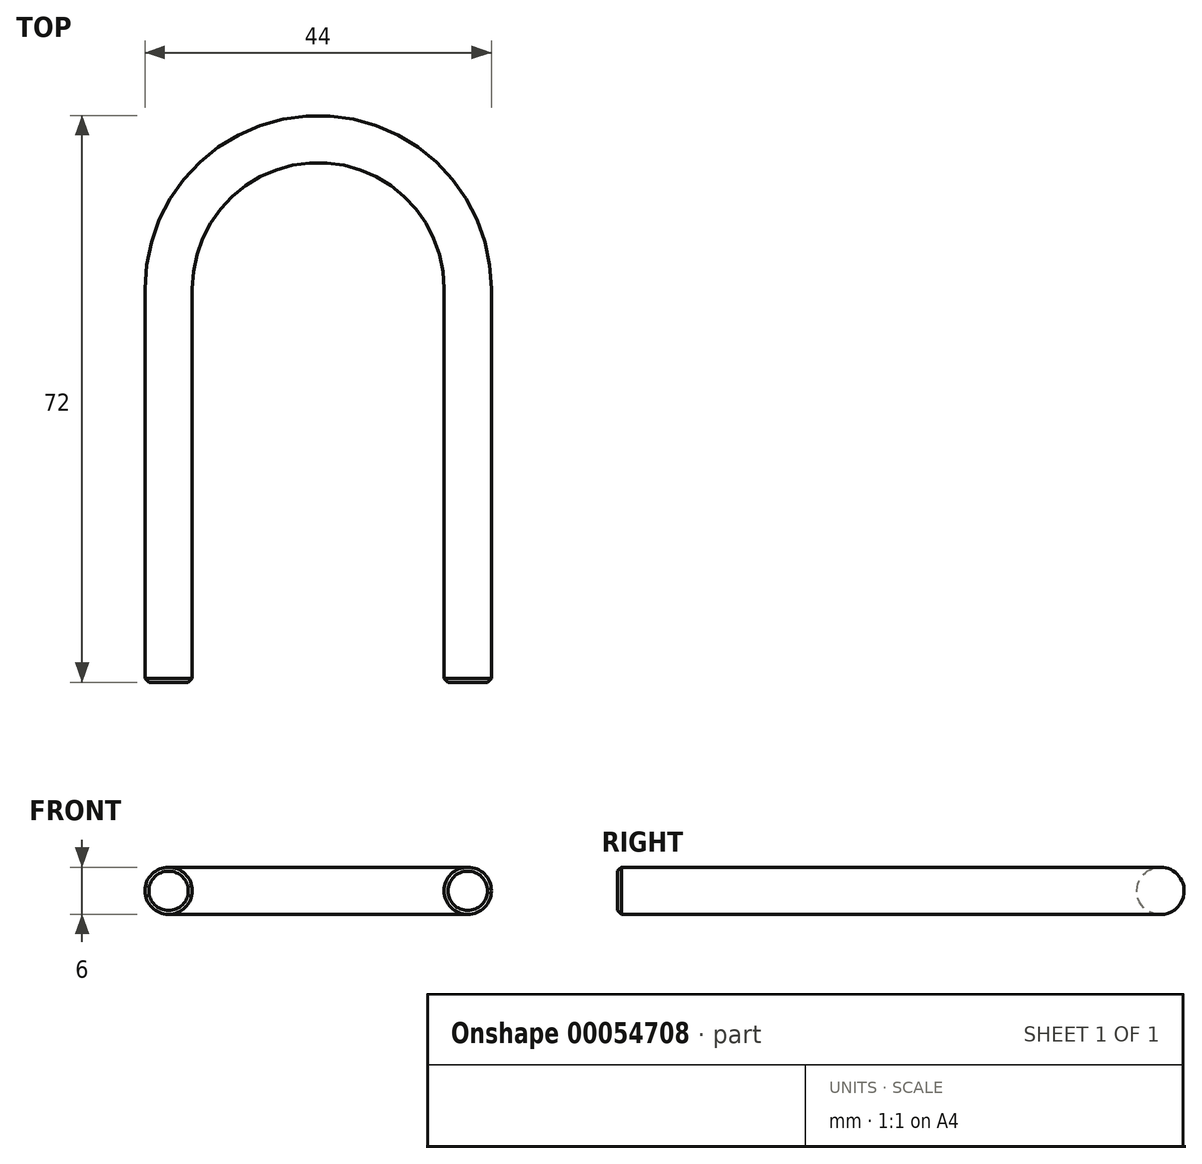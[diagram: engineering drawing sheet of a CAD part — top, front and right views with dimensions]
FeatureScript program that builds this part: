
annotation { "Feature Type Name" : "Feature", "Feature Type Description" : "" }
export const myFeature = defineFeature(function(context is Context, id is Id, definition is map)
    precondition{}
    {
        {
            var Q0;
            Q0=qCreatedBy(makeId("Top.planeOp"),FACE);
            var sketch = newSketch(context, id + "F0", { "sketchPlane" : qUnion([Q0])});
            skArc(sketch, "E0", {"start": v(19, 0) * mm, "mid": v(0, 19) * mm, "end": v(-19, 0) * mm});
            skLineSegment(sketch, "E1", {"start": v(-19, 0) * mm, "end": v(-19, -50) * mm});
            skLineSegment(sketch, "E2", {"start": v(19, 0) * mm, "end": v(19, -50) * mm});
            skSolve(sketch);
        }
        {
            var Q0;
            Q0=sQuery(id+"F0.wireOp",VERTEX,"E1.end");
            var Q1;
            Q1=qCreatedBy(makeId("Front.planeOp"),FACE);
            cPlane(context, id + "F1", {"entities" : qUnion([Q0, Q1]), "cplaneType" : CPlaneType.PLANE_POINT, "offset" : 50 * mm, "width" : 150 * mm, "height" : 150 * mm});
        }
        {
            var Q0;
            Q0=qCreatedBy(id+"F1.planeOp",FACE);
            var sketch = newSketch(context, id + "F2", { "sketchPlane" : qUnion([Q0])});
            skCircle(sketch, "E3", {"center": v(-19, 0) * mm, "radius": 3 * mm});
            skSolve(sketch);
        }
        {
            var Q0;
            Q0=makeQuery(id+"F2.imprint","IMPRINT",FACE,{"disambiguationData":[TD([[makeQuery(id+"F2.imprint","IMPRINT",EDGE,{"derivedFrom":sQuery(id+"F2.wireOp",EDGE,"E3")}),1.0]])]});
            var Q1;
            Q1=sQuery(id+"F0.wireOp",EDGE,"E1");
            var Q2;
            Q2=sQuery(id+"F0.wireOp",EDGE,"E0");
            var Q3;
            Q3=sQuery(id+"F0.wireOp",EDGE,"E2");
            sweep(context, id + "F3", {"profiles" : qUnion([Q0]), "path" : qUnion([Q1, Q2, Q3])});
        }
        {
            var Q0;
            Q0=makeQuery(id+"F3.opSweep","CAP_EDGE",EDGE,{"disambiguationData":[OSD([sQuery(id+"F0.wireOp",VERTEX,"E1.end"),sQuery(id+"F2.wireOp",EDGE,"E3")])],"isStart":true});
            var Q1;
            Q1=makeQuery(id+"F3.opSweep","CAP_EDGE",EDGE,{"disambiguationData":[OSD([sQuery(id+"F0.wireOp",VERTEX,"E2.end"),sQuery(id+"F2.wireOp",EDGE,"E3")])],"isStart":false});
            chamfer(context, id + "F4", {"entities" : qUnion([Q0, Q1]), "width" : .5 * mm, "tangentPropagation" : true});
        }
    });
